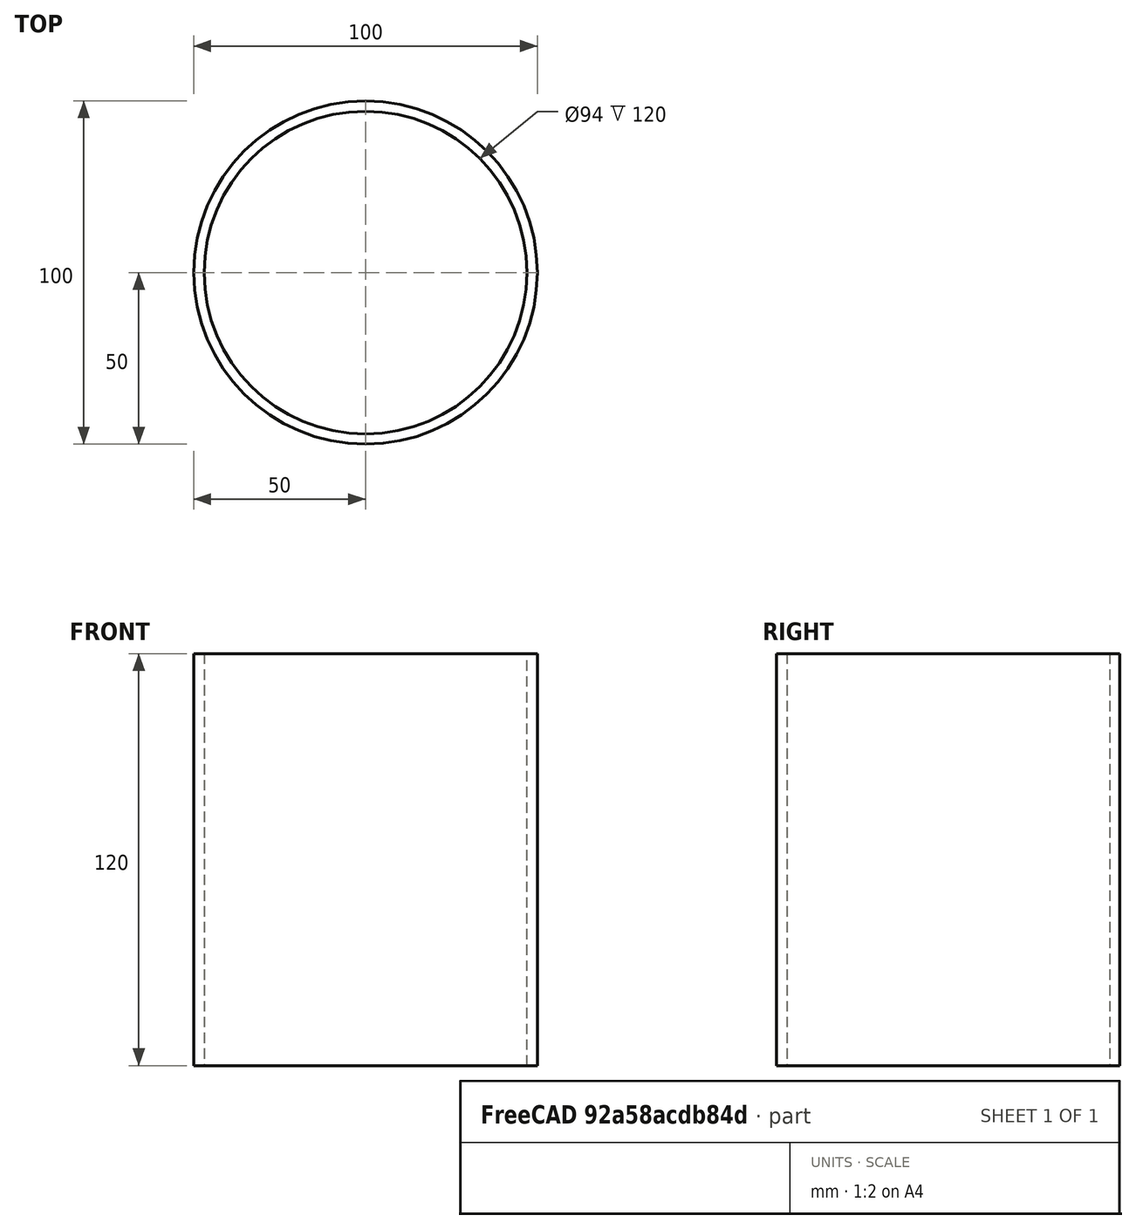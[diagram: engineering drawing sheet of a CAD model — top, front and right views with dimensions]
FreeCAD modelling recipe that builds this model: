
FCSTD DOCUMENT  (FreeCAD 0.16R6706 (Git))
Label: acrylic_tube
License: All rights reserved
LicenseURL: http://en.wikipedia.org/wiki/All_rights_reserved
objects: Sketcher::SketchObject×1, PartDesign::Pad×1
note: 3 computed .brp shape members not serialized (recipe doc carries the construction recipe); baked Part::Feature solids carry a one-line shape summary decoded from their .brp

FEATURE [Sketcher::SketchObject] Sketch
  sketch-geometry (3):
    g0: Circle CenterX=0 CenterY=0 CenterZ=0 NormalX=0 NormalY=0 NormalZ=1 Radius=50
    g1: Circle CenterX=0 CenterY=0 CenterZ=0 NormalX=0 NormalY=0 NormalZ=1 Radius=47
    g2: LineSegment [constr] StartX=0.284691 StartY=46.9991 StartZ=0 EndX=0.302863 EndY=49.9991 EndZ=0
  constraints (7):
    c: Coincident(g0,g-1)
    c: Coincident(g1,g-1)
    c: Radius(g0) = 50
    c: PointOnObject(g2,g1)
    c: PointOnObject(g2,g0)
    c: Perpendicular(g1,g2)
    c: Distance(g2) = 3
FEATURE [PartDesign::Pad] Pad
  Length = 120
  Length2 = 100
  Sketch = -> Sketch
  Type = 0
